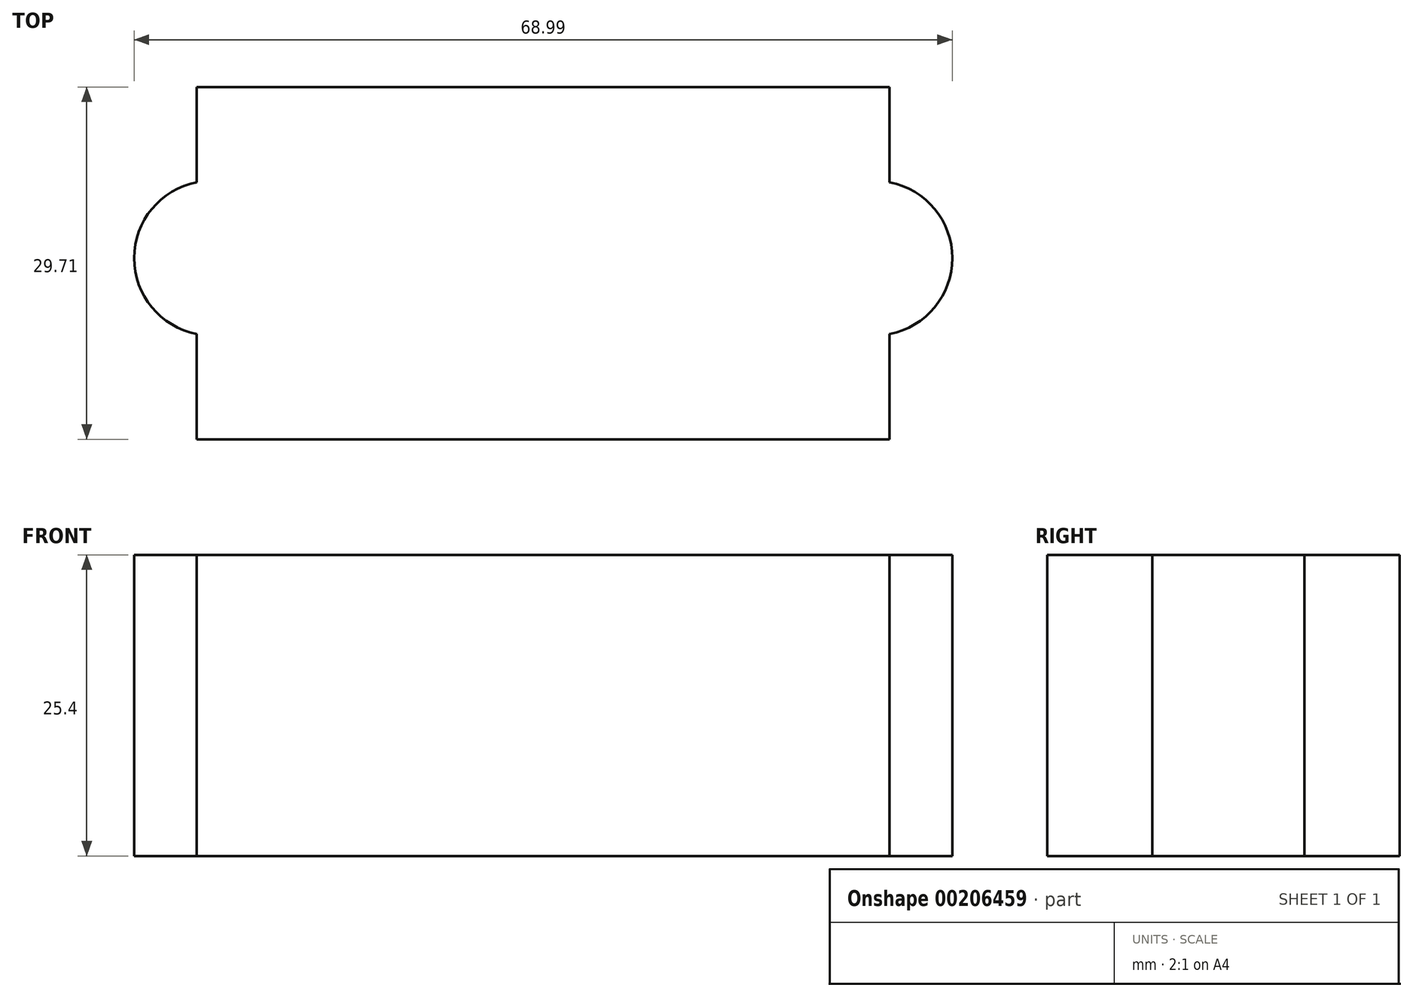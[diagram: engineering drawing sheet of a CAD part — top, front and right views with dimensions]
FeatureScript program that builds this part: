
annotation { "Feature Type Name" : "Feature", "Feature Type Description" : "" }
export const myFeature = defineFeature(function(context is Context, id is Id, definition is map)
    precondition{}
    {
        {
            var Q0;
            Q0=qCreatedBy(makeId("Top.planeOp"),FACE);
            var sketch = newSketch(context, id + "F0", { "sketchPlane" : qUnion([Q0])});
            skLineSegment(sketch, "E0.bottom", {"start": v(-47.86, 29.71) * mm, "end": v(10.56, 29.71) * mm});
            skLineSegment(sketch, "E0.top", {"start": v(-47.86, 0) * mm, "end": v(10.56, 0) * mm});
            skLineSegment(sketch, "E0.left", {"start": v(-47.86, 29.71) * mm, "end": v(-47.86, 0) * mm});
            skLineSegment(sketch, "E0.right", {"start": v(10.56, 29.71) * mm, "end": v(10.56, 0) * mm});
            skPoint(sketch, "E1", {"position": v(-47.86, 14.86) * mm});
            skArc(sketch, "E2", {"start": v(-47.86, 21.68) * mm, "mid": v(-53.15, 15.28) * mm, "end": v(-47.86, 8.88) * mm});
            skLineSegment(sketch, "E3", {"start": v(-18.65, 29.71) * mm, "end": v(-18.65, 0) * mm, "construction": true});
            skArc(sketch, "E4.MirrorCS", {"start": v(10.56, 21.68) * mm, "mid": v(15.84, 15.28) * mm, "end": v(10.56, 8.88) * mm});
            skSolve(sketch);
        }
        {
            var Q0;
            Q0 = qSketchRegion(id + "F0", true);
            var Q1;
            Q1=sQuery(id+"F0.wireOp",EDGE,"E2");
            var Q2;
            Q2=sQuery(id+"F0.wireOp",EDGE,"E0.left");
            var Q3;
            Q3=sQuery(id+"F0.wireOp",EDGE,"E0.bottom");
            var Q4;
            Q4=sQuery(id+"F0.wireOp",EDGE,"E0.top");
            var Q5;
            Q5=sQuery(id+"F0.wireOp",EDGE,"E0.right");
            var Q6;
            Q6=sQuery(id+"F0.wireOp",EDGE,"E4.MirrorCS");
            extrude(context, id + "F1", {"entities" : qUnion([Q0]), "surfaceEntities" : qUnion([Q1, Q2, Q3, Q4, Q5, Q6]), "depth" : 25.4 * mm});
        }
    });
